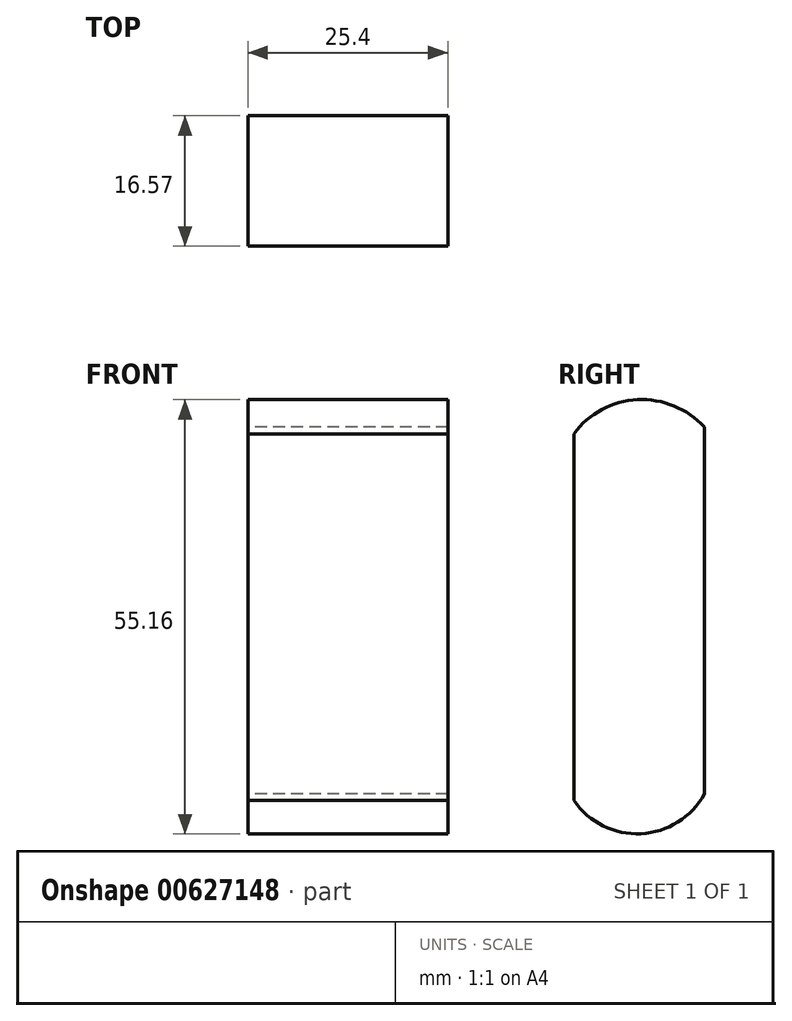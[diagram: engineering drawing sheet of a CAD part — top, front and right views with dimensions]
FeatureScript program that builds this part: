
annotation { "Feature Type Name" : "Feature", "Feature Type Description" : "" }
export const myFeature = defineFeature(function(context is Context, id is Id, definition is map)
    precondition{}
    {
        {
            var Q0;
            Q0=qCreatedBy(makeId("Right.planeOp"),FACE);
            var sketch = newSketch(context, id + "F0", { "sketchPlane" : qUnion([Q0])});
            skArc(sketch, "E0", {"start": v(6.88, 28.5) * mm, "mid": v(-1.6, 31.98) * mm, "end": v(-9.69, 27.65) * mm});
            skLineSegment(sketch, "E1", {"start": v(-9.69, 27.65) * mm, "end": v(-9.69, -18.95) * mm});
            skLineSegment(sketch, "E2", {"start": v(6.88, 28.5) * mm, "end": v(6.88, -18.11) * mm});
            skArc(sketch, "E3", {"start": v(-9.69, -18.95) * mm, "mid": v(-1.17, -23.15) * mm, "end": v(6.88, -18.11) * mm});
            skSolve(sketch);
        }
        {
            var Q0;
            Q0 = qSketchRegion(id + "F0", true);
            extrude(context, id + "F1", {"entities" : qUnion([Q0]), "depth" : 25.4 * mm, "offsetDistance" : 25.4 * mm});
        }
    });
